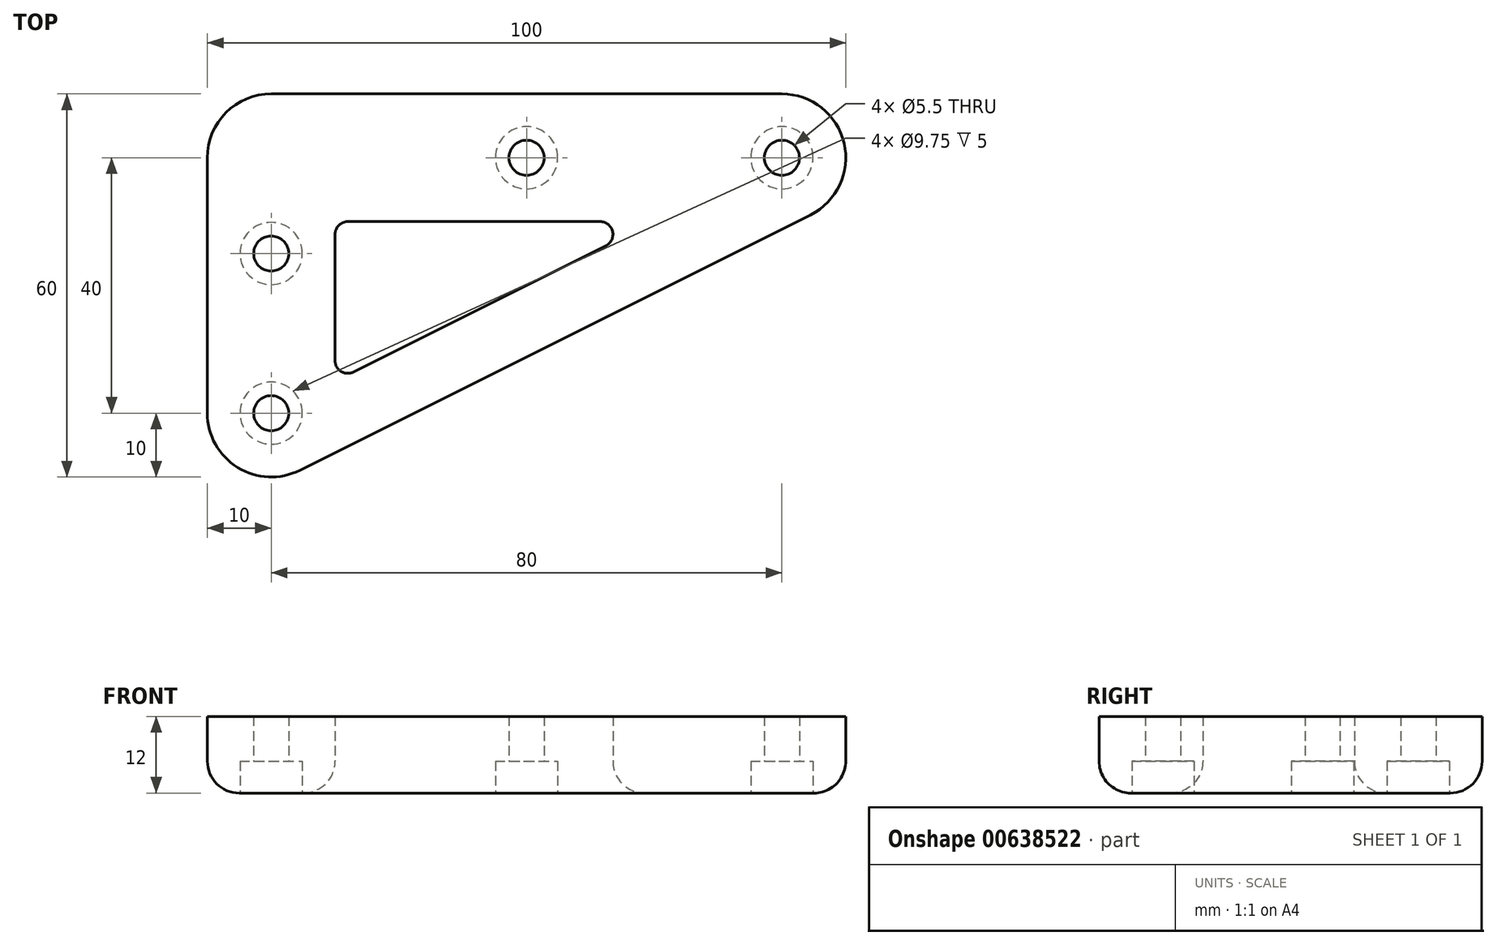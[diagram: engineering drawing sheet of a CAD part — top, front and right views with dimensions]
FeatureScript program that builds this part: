
annotation { "Feature Type Name" : "Feature", "Feature Type Description" : "" }
export const myFeature = defineFeature(function(context is Context, id is Id, definition is map)
    precondition{}
    {
        {
            var Q0;
            Q0=qCreatedBy(makeId("Top.planeOp"),FACE);
            var sketch = newSketch(context, id + "F0", { "sketchPlane" : qUnion([Q0])});
            skArc(sketch, "E0", {"start": v(0, 10) * mm, "mid": v(-7.07, 7.07) * mm, "end": v(-10, 0) * mm});
            skArc(sketch, "E1", {"start": v(84.47, -8.94) * mm, "mid": v(89.73, 2.3) * mm, "end": v(80, 10) * mm});
            skArc(sketch, "E2", {"start": v(-10, -40) * mm, "mid": v(-5.26, -48.5) * mm, "end": v(4.47, -48.94) * mm});
            skLineSegment(sketch, "E3", {"start": v(-10, 0) * mm, "end": v(-10, -40) * mm});
            skLineSegment(sketch, "E4", {"start": v(0, 10) * mm, "end": v(80, 10) * mm});
            skLineSegment(sketch, "E5", {"start": v(84.47, -8.94) * mm, "end": v(4.47, -48.94) * mm});
            skPoint(sketch, "E6", {"position": v(40, 0) * mm});
            skLineSegment(sketch, "E7.0", {"start": v(52.42, -13.79) * mm, "end": v(12.9, -33.55) * mm});
            skLineSegment(sketch, "E8.0", {"start": v(12, -10) * mm, "end": v(51.53, -10) * mm});
            skLineSegment(sketch, "E9.0", {"start": v(10, -12) * mm, "end": v(10, -31.76) * mm});
            skPoint(sketch, "E10.visualSharp", {"position": v(10, -10) * mm});
            skArc(sketch, "E10.filletArc", {"start": v(12, -10) * mm, "mid": v(10.59, -10.59) * mm, "end": v(10, -12) * mm});
            skPoint(sketch, "E11.visualSharp", {"position": v(10, -35) * mm});
            skArc(sketch, "E11.filletArc", {"start": v(10, -31.76) * mm, "mid": v(10.95, -33.47) * mm, "end": v(12.9, -33.55) * mm});
            skPoint(sketch, "E12.visualSharp", {"position": v(60, -10) * mm});
            skArc(sketch, "E12.filletArc", {"start": v(52.42, -13.79) * mm, "mid": v(53.47, -11.54) * mm, "end": v(51.53, -10) * mm});
            skPoint(sketch, "E13", {"position": v(0, -15) * mm});
            skSolve(sketch);
        }
        {
            var Q0;
            Q0=makeQuery(id+"F0.imprint","IMPRINT",FACE,{"disambiguationData":[TD([[makeQuery(id+"F0.imprint","IMPRINT",EDGE,{"derivedFrom":sQuery(id+"F0.wireOp",EDGE,"E0")}),1.0]])]});
            extrude(context, id + "F1", {"entities" : qUnion([Q0]), "depth" : 12 * mm, "offsetDistance" : 25 * mm});
        }
        {
            var Q0;
            Q0=sQuery(id+"F0.wireOp",VERTEX,"E1.center");
            var Q1;
            Q1=sQuery(id+"F0.wireOp",VERTEX,"E2.center");
            var Q2;
            Q2=sQuery(id+"F0.wireOp",VERTEX,"E6");
            var Q3;
            Q3=sQuery(id+"F0.wireOp",VERTEX,"E13");
            var Q4;
            Q4=makeQuery(id+"F1.opExtrude","SWEPT_BODY",BODY,{"disambiguationData":[OSD([sQuery(id+"F0.wireOp",EDGE,"E0"),sQuery(id+"F0.wireOp",EDGE,"E1"),sQuery(id+"F0.wireOp",EDGE,"E2"),sQuery(id+"F0.wireOp",EDGE,"E3"),sQuery(id+"F0.wireOp",EDGE,"E4"),sQuery(id+"F0.wireOp",EDGE,"E5"),sQuery(id+"F0.wireOp",EDGE,"E7.0"),sQuery(id+"F0.wireOp",EDGE,"E8.0"),sQuery(id+"F0.wireOp",EDGE,"E9.0"),sQuery(id+"F0.wireOp",EDGE,"E10.filletArc"),sQuery(id+"F0.wireOp",EDGE,"E11.filletArc"),sQuery(id+"F0.wireOp",EDGE,"E12.filletArc")])]});
            hole(context, id + "F2", {"style" : HoleStyle.C_BORE, "endStyle" : HoleEndStyle.THROUGH, "oppositeDirection" : true, "standardTappedOrClearance" : lookupTablePath({ "standard" : "ISO", "fit" : "Normal", "size" : "M5", "type" : "Clearance" }), "standardBlindInLast" : lookupTablePath({ "fit" : "Standard", "standard" : "ISO", "size" : "M5", "type" : "Clearance" }), "holeDiameter" : 5.5 * mm, "cBoreDiameter" : 9.75 * mm, "cBoreDepth" : 5 * mm, "majorDiameter" : 5 * mm, "isTappedThrough" : true, "tappedDepth" : 12 * mm, "tapClearance" : 3, "locations" : qUnion([Q0, Q1, Q2, Q3]), "scope" : qUnion([Q4])});
        }
        {
            var Q0;
            Q0=makeQuery(id+"F1.opExtrude","CAP_EDGE",EDGE,{"disambiguationData":[OSD([sQuery(id+"F0.wireOp",EDGE,"E5")])],"isStart":true});
            var Q1;
            Q1=makeQuery(id+"F1.opExtrude","CAP_EDGE",EDGE,{"disambiguationData":[OSD([sQuery(id+"F0.wireOp",EDGE,"E8.0")])],"isStart":true});
            fillet(context, id + "F3", {"entities" : qUnion([Q0, Q1]), "radius" : 5 * mm, "tangentPropagation" : true, "allowEdgeOverflow" : false});
        }
    });
